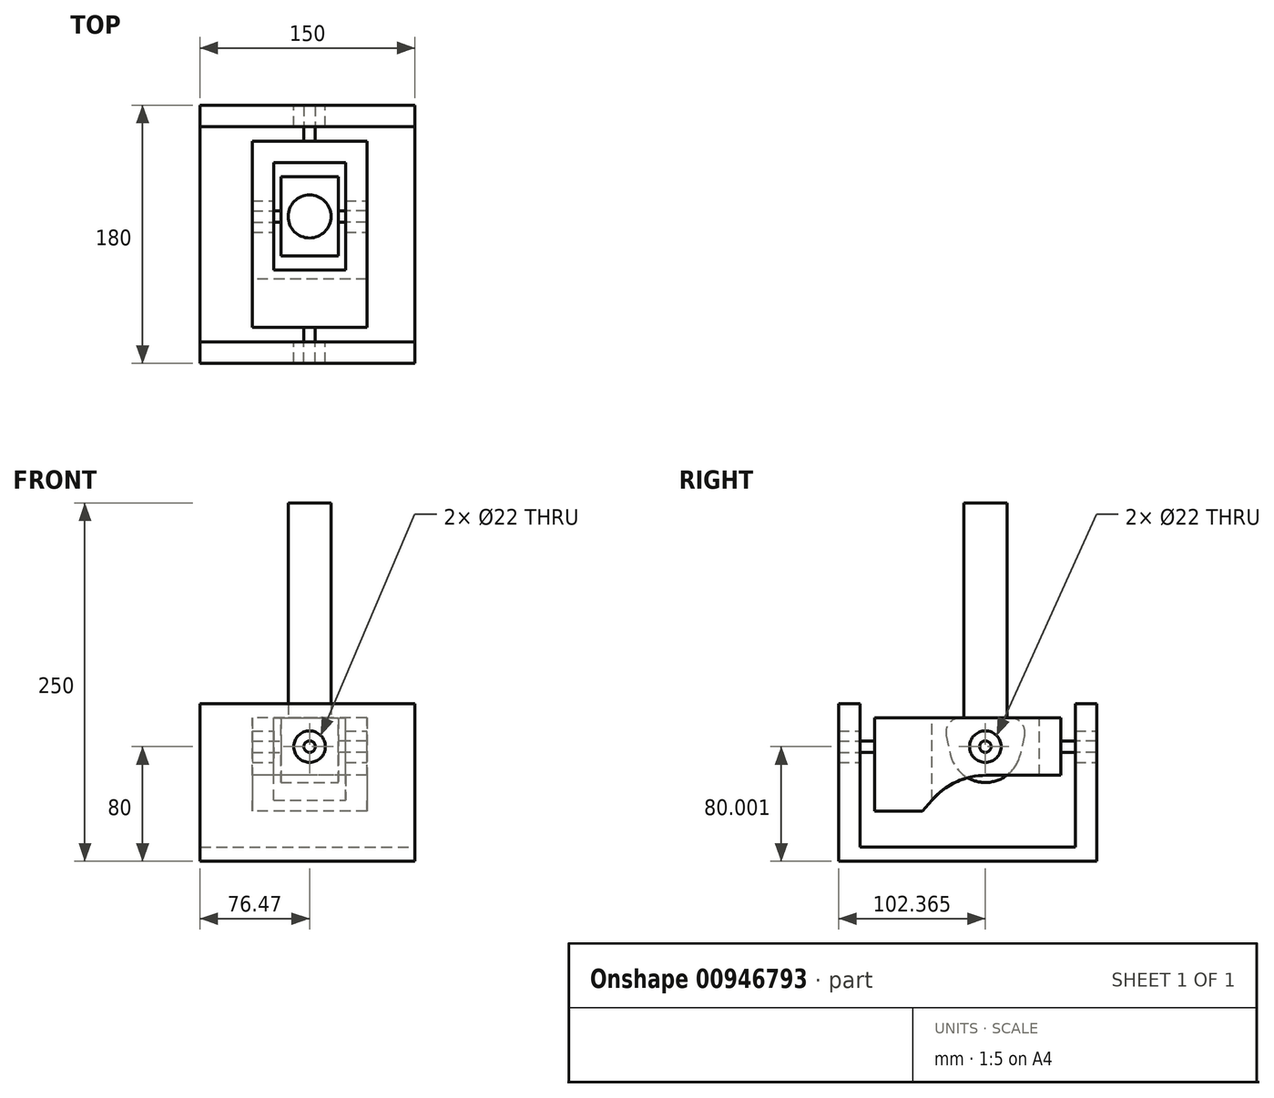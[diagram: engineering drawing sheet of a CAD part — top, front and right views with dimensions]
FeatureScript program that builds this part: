
annotation { "Feature Type Name" : "Feature", "Feature Type Description" : "" }
export const myFeature = defineFeature(function(context is Context, id is Id, definition is map)
    precondition{}
    {
        {
            var Q0;
            Q0=qCreatedBy(makeId("Top.planeOp"),FACE);
            var sketch = newSketch(context, id + "F0", { "sketchPlane" : qUnion([Q0])});
            skLineSegment(sketch, "E0", {"start": v(-76.47, 69.91) * mm, "end": v(-76.47, -110.09) * mm});
            skLineSegment(sketch, "E1", {"start": v(-76.47, -110.09) * mm, "end": v(73.53, -110.09) * mm});
            skLineSegment(sketch, "E2", {"start": v(73.53, -110.09) * mm, "end": v(73.53, 69.91) * mm});
            skLineSegment(sketch, "E3", {"start": v(73.53, 69.91) * mm, "end": v(-76.47, 69.91) * mm});
            skSolve(sketch);
        }
        {
            var Q0;
            Q0=makeQuery(id+"F0.imprint","IMPRINT",FACE,{"disambiguationData":[TD([[makeQuery(id+"F0.imprint","IMPRINT",EDGE,{"derivedFrom":sQuery(id+"F0.wireOp",EDGE,"E0")}),1.0]])]});
            extrude(context, id + "F1", {"entities" : qUnion([Q0]), "depth" : 10 * mm, "offsetDistance" : 25.4 * mm});
        }
        {
            var Q0;
            Q0=makeQuery(id+"F1.opExtrude","CAP_FACE",FACE,{"disambiguationData":[OSD([sQuery(id+"F0.wireOp",EDGE,"E0"),sQuery(id+"F0.wireOp",EDGE,"E1"),sQuery(id+"F0.wireOp",EDGE,"E2"),sQuery(id+"F0.wireOp",EDGE,"E3")])],"isStart":false});
            var sketch = newSketch(context, id + "F2", { "sketchPlane" : qUnion([Q0])});
            skLineSegment(sketch, "E4", {"start": v(73.53, 54.91) * mm, "end": v(-76.47, 54.91) * mm});
            skLineSegment(sketch, "E5", {"start": v(-76.47, -95.09) * mm, "end": v(73.53, -95.09) * mm});
            skSolve(sketch);
        }
        {
            var Q0;
            {var subQ0=sQuery(id+"F2.wireOp",EDGE,"E4");Q0=makeQuery(id+"F2.imprint","IMPRINT",FACE,{"disambiguationData":[TD([[makeQuery(id+"F2.imprint","IMPRINT",EDGE,{"derivedFrom":subQ0}),-1.0]])]});}
            var Q1;
            {var subQ0=sQuery(id+"F2.wireOp",EDGE,"E5");Q1=makeQuery(id+"F2.imprint","IMPRINT",FACE,{"disambiguationData":[TD([[makeQuery(id+"F2.imprint","IMPRINT",EDGE,{"derivedFrom":subQ0}),-1.0]])]});}
            extrude(context, id + "F3", {"entities" : qUnion([Q0, Q1]), "operationType" : NewBodyOperationType.ADD, "depth" : 100 * mm, "offsetDistance" : 25.4 * mm});
        }
        {
            var Q0;
            {var subQ0=sQuery(id+"F0.wireOp",EDGE,"E3");Q0=makeQuery(id+"F3.boolean.opBoolean","MERGE",FACE,{"derivedFrom":[makeQuery(id+"F1.opExtrude","SWEPT_FACE",FACE,{"disambiguationData":[OSD([subQ0])]}),makeQuery(id+"F3.opExtrude","SWEPT_FACE",FACE,{"disambiguationData":[OSD([subQ0])]})]});}
            var sketch = newSketch(context, id + "F4", { "sketchPlane" : qUnion([Q0])});
            skCircle(sketch, "E6", {"center": v(0, 80) * mm, "radius": 11 * mm});
            skSolve(sketch);
        }
        {
            var Q0;
            Q0=sQuery(id+"F4.wireOp",VERTEX,"E6.center");
            var Q1;
            Q1=makeQuery(id+"F1.opExtrude","SWEPT_BODY",BODY,{"disambiguationData":[OSD([sQuery(id+"F0.wireOp",EDGE,"E0"),sQuery(id+"F0.wireOp",EDGE,"E1"),sQuery(id+"F0.wireOp",EDGE,"E2"),sQuery(id+"F0.wireOp",EDGE,"E3")])]});
            hole(context, id + "F5", {"style" : HoleStyle.SIMPLE, "endStyle" : HoleEndStyle.THROUGH, "holeDiameter" : 22 * mm, "majorDiameter" : 6.35 * mm, "isTappedThrough" : true, "tappedDepth" : 12.7 * mm, "tapClearance" : 3, "locations" : qUnion([Q0]), "scope" : qUnion([Q1])});
        }
        {
            var Q0;
            Q0=qCreatedBy(makeId("Right.planeOp"),FACE);
            var sketch = newSketch(context, id + "F6", { "sketchPlane" : qUnion([Q0])});
            skLineSegment(sketch, "E7", {"start": v(-85.09, 100) * mm, "end": v(-85.09, 35) * mm});
            skLineSegment(sketch, "E8", {"start": v(-85.09, 35) * mm, "end": v(44.91, 35) * mm});
            skLineSegment(sketch, "E9", {"start": v(44.91, 35) * mm, "end": v(44.91, 100) * mm});
            skLineSegment(sketch, "E10", {"start": v(44.91, 100) * mm, "end": v(-85.09, 100) * mm});
            skLineSegment(sketch, "E11", {"start": v(-51.54, 35) * mm, "end": v(-45.05, 42.56) * mm});
            skLineSegment(sketch, "E12", {"start": v(-7.1, 60) * mm, "end": v(44.91, 60) * mm});
            skPoint(sketch, "E12.endSnap0", {"position": v(44.91, 67.5) * mm});
            skPoint(sketch, "E13.visualSharp", {"position": v(-30.09, 60) * mm});
            skArc(sketch, "E13.filletArc", {"start": v(-7.1, 60) * mm, "mid": v(-27.99, 55.43) * mm, "end": v(-45.05, 42.56) * mm});
            skSolve(sketch);
        }
        {
            var Q0;
            {var subQ4=sQuery(id+"F6.wireOp",EDGE,"E7");Q0=makeQuery(id+"F6.imprint","IMPRINT",FACE,{"disambiguationData":[TD([[makeQuery(id+"F6.imprint","IMPRINT",EDGE,{"derivedFrom":subQ4}),1.0]])]});}
            extrude(context, id + "F7", {"entities" : qUnion([Q0]), "depth" : 40 * mm, "offsetDistance" : 25.4 * mm});
        }
        {
            var Q0;
            Q0=makeQuery(id+"F7.opExtrude","SWEPT_BODY",BODY,{"disambiguationData":[OSD([sQuery(id+"F6.wireOp",EDGE,"E7"),sQuery(id+"F6.wireOp",EDGE,"E8"),sQuery(id+"F6.wireOp",EDGE,"E9"),sQuery(id+"F6.wireOp",EDGE,"E10"),sQuery(id+"F6.wireOp",EDGE,"E11"),sQuery(id+"F6.wireOp",EDGE,"E12"),sQuery(id+"F6.wireOp",EDGE,"E13.filletArc")])]});
            var Q1;
            Q1=qCreatedBy(makeId("Right.planeOp"),FACE);
            mirror(context, id + "F8", {"operationType" : NewBodyOperationType.ADD, "entities" : qUnion([Q0]), "mirrorPlane" : qUnion([Q1])});
        }
        {
            var Q0;
            {var subQ0=makeQuery(id+"F7.opExtrude","SWEPT_FACE",FACE,{"disambiguationData":[OSD([sQuery(id+"F6.wireOp",EDGE,"E7")])]});Q0=makeQuery(id+"F8.boolean.opBoolean","MERGE",FACE,{"derivedFrom":[subQ0,makeQuery(id+"F8.opPattern","COPY",FACE,{"derivedFrom":subQ0,"instanceName":"1"})]});}
            var sketch = newSketch(context, id + "F9", { "sketchPlane" : qUnion([Q0])});
            skCircle(sketch, "E14", {"center": v(0, 80.04) * mm, "radius": 4 * mm});
            skSolve(sketch);
        }
        {
            var Q0;
            Q0=makeQuery(id+"F9.imprint","IMPRINT",FACE,{"disambiguationData":[TD([[makeQuery(id+"F9.imprint","IMPRINT",EDGE,{"derivedFrom":sQuery(id+"F9.wireOp",EDGE,"E14")}),1.0]])]});
            extrude(context, id + "F10", {"entities" : qUnion([Q0]), "operationType" : NewBodyOperationType.ADD, "depth" : 25 * mm, "offsetDistance" : 25.4 * mm});
        }
        {
            var Q0;
            {var subQ0=makeQuery(id+"F7.opExtrude","SWEPT_FACE",FACE,{"disambiguationData":[OSD([sQuery(id+"F6.wireOp",EDGE,"E9")])]});Q0=makeQuery(id+"F8.boolean.opBoolean","MERGE",FACE,{"derivedFrom":[subQ0,makeQuery(id+"F8.opPattern","COPY",FACE,{"derivedFrom":subQ0,"instanceName":"1"})]});}
            var sketch = newSketch(context, id + "F11", { "sketchPlane" : qUnion([Q0])});
            skCircle(sketch, "E15", {"center": v(0, 80) * mm, "radius": 4 * mm});
            skPoint(sketch, "E15.centerSnap0", {"position": v(-40, 80) * mm});
            skSolve(sketch);
        }
        {
            var Q0;
            Q0=makeQuery(id+"F11.imprint","IMPRINT",FACE,{"disambiguationData":[TD([[makeQuery(id+"F11.imprint","IMPRINT",EDGE,{"derivedFrom":sQuery(id+"F11.wireOp",EDGE,"E15")}),1.0]])]});
            extrude(context, id + "F12", {"entities" : qUnion([Q0]), "operationType" : NewBodyOperationType.ADD, "depth" : 25 * mm, "offsetDistance" : 25.4 * mm});
        }
        {
            var Q0;
            {var subQ0=makeQuery(id+"F7.opExtrude","SWEPT_FACE",FACE,{"disambiguationData":[OSD([sQuery(id+"F6.wireOp",EDGE,"E10")])]});Q0=makeQuery(id+"F8.boolean.opBoolean","MERGE",FACE,{"derivedFrom":[subQ0,makeQuery(id+"F8.opPattern","COPY",FACE,{"derivedFrom":subQ0,"instanceName":"1"})]});}
            var sketch = newSketch(context, id + "F13", { "sketchPlane" : qUnion([Q0])});
            skLineSegment(sketch, "E16", {"start": v(-25, -45.09) * mm, "end": v(25, -45.09) * mm});
            skLineSegment(sketch, "E17", {"start": v(25, -45.09) * mm, "end": v(25, 29.91) * mm});
            skLineSegment(sketch, "E18", {"start": v(25, 29.91) * mm, "end": v(-25, 29.91) * mm});
            skLineSegment(sketch, "E19", {"start": v(-25, 29.91) * mm, "end": v(-25, -45.09) * mm});
            skSolve(sketch);
        }
        {
            var Q0;
            Q0=makeQuery(id+"F13.imprint","IMPRINT",FACE,{"disambiguationData":[TD([[makeQuery(id+"F13.imprint","IMPRINT",EDGE,{"derivedFrom":sQuery(id+"F13.wireOp",EDGE,"E16")}),1.0]])]});
            extrude(context, id + "F14", {"entities" : qUnion([Q0]), "operationType" : NewBodyOperationType.REMOVE, "oppositeDirection" : true, "depth" : 65.28 * mm, "offsetDistance" : 25.4 * mm});
        }
        {
            var Q0;
            {var subQ0=makeQuery(id+"F7.opExtrude","SWEPT_FACE",FACE,{"disambiguationData":[OSD([sQuery(id+"F6.wireOp",EDGE,"E10")])]});Q0=makeQuery(id+"F8.boolean.opBoolean","MERGE",FACE,{"derivedFrom":[subQ0,makeQuery(id+"F8.opPattern","COPY",FACE,{"derivedFrom":subQ0,"instanceName":"1"})]});}
            var sketch = newSketch(context, id + "F15", { "sketchPlane" : qUnion([Q0])});
            skLineSegment(sketch, "E20", {"start": v(25, -7.59) * mm, "end": v(40, -7.59) * mm});
            skSolve(sketch);
        }
        {
            var Q0;
            Q0=makeQuery(id+"F7.opExtrude","CAP_FACE",FACE,{"disambiguationData":[OSD([sQuery(id+"F6.wireOp",EDGE,"E7"),sQuery(id+"F6.wireOp",EDGE,"E8"),sQuery(id+"F6.wireOp",EDGE,"E9"),sQuery(id+"F6.wireOp",EDGE,"E10"),sQuery(id+"F6.wireOp",EDGE,"E11"),sQuery(id+"F6.wireOp",EDGE,"E12"),sQuery(id+"F6.wireOp",EDGE,"E13.filletArc")])],"isStart":false});
            var sketch = newSketch(context, id + "F16", { "sketchPlane" : qUnion([Q0])});
            skCircle(sketch, "E21", {"center": v(-7.72, 80) * mm, "radius": 11 * mm});
            skSolve(sketch);
        }
        {
            var Q0;
            Q0=makeQuery(id+"F16.imprint","IMPRINT",FACE,{"disambiguationData":[TD([[makeQuery(id+"F16.imprint","IMPRINT",EDGE,{"derivedFrom":sQuery(id+"F16.wireOp",EDGE,"E21")}),1.0]])]});
            extrude(context, id + "F17", {"entities" : qUnion([Q0]), "operationType" : NewBodyOperationType.REMOVE, "oppositeDirection" : true, "depth" : 87.12 * mm, "offsetDistance" : 25.4 * mm});
        }
        {
            var Q0;
            Q0=makeQuery(id+"F7.opExtrude","CAP_FACE",FACE,{"disambiguationData":[OSD([sQuery(id+"F6.wireOp",EDGE,"E7"),sQuery(id+"F6.wireOp",EDGE,"E8"),sQuery(id+"F6.wireOp",EDGE,"E9"),sQuery(id+"F6.wireOp",EDGE,"E10"),sQuery(id+"F6.wireOp",EDGE,"E11"),sQuery(id+"F6.wireOp",EDGE,"E12"),sQuery(id+"F6.wireOp",EDGE,"E13.filletArc")])],"isStart":false});
            var sketch = newSketch(context, id + "F18", { "sketchPlane" : qUnion([Q0])});
            skCircle(sketch, "E22", {"center": v(-7.72, 80) * mm, "radius": 4 * mm});
            skSolve(sketch);
        }
        {
            var Q0;
            {var subQ1=sQuery(id+"F6.wireOp",EDGE,"E10");var subQ6=makeQuery(id+"F7.opExtrude","CAP_EDGE",EDGE,{"disambiguationData":[OSD([subQ1])],"isStart":false});Q0=makeQuery(id+"F15.imprint","IMPRINT",FACE,{"disambiguationData":[TD([[makeQuery(id+"F15.imprint","IMPRINT",EDGE,{"derivedFrom":makeQuery(id+"F8.opPattern","COPY",EDGE,{"derivedFrom":subQ6,"instanceName":"1"})}),1.0]])]});}
            var sketch = newSketch(context, id + "F19", { "sketchPlane" : qUnion([Q0])});
            skLineSegment(sketch, "E23", {"start": v(-20, 22.41) * mm, "end": v(20, 22.41) * mm});
            skLineSegment(sketch, "E24", {"start": v(20, 22.41) * mm, "end": v(20, -37.59) * mm});
            skLineSegment(sketch, "E25", {"start": v(20, -37.59) * mm, "end": v(-20, -37.59) * mm});
            skLineSegment(sketch, "E26", {"start": v(-20, -37.59) * mm, "end": v(-20, 22.41) * mm});
            skSolve(sketch);
        }
        {
            var Q0;
            Q0=makeQuery(id+"F19.imprint","IMPRINT",FACE,{"disambiguationData":[TD([[makeQuery(id+"F19.imprint","IMPRINT",EDGE,{"derivedFrom":sQuery(id+"F19.wireOp",EDGE,"E23")}),-1.0]])]});
            extrude(context, id + "F20", {"entities" : qUnion([Q0]), "oppositeDirection" : true, "depth" : 45 * mm, "offsetDistance" : 25.4 * mm});
        }
        {
            var Q0;
            Q0=makeQuery(id+"F20.opExtrude","SWEPT_FACE",FACE,{"disambiguationData":[OSD([sQuery(id+"F19.wireOp",EDGE,"E24")])]});
            var sketch = newSketch(context, id + "F21", { "sketchPlane" : qUnion([Q0])});
            skPoint(sketch, "E27.endSnap0", {"position": v(-7.59, 55) * mm});
            skPoint(sketch, "E28", {"position": v(-7.72, 80) * mm});
            skCircle(sketch, "E29", {"center": v(-7.72, 80) * mm, "radius": 25 * mm});
            skLineSegment(sketch, "E30", {"start": v(19.66, 87.8) * mm, "end": v(16.66, 74.5) * mm});
            skLineSegment(sketch, "E31", {"start": v(-34.99, 87.9) * mm, "end": v(-32.17, 74.76) * mm});
            skLineSegment(sketch, "E32", {"start": v(-25.21, 100) * mm, "end": v(9.9, 100) * mm});
            skPoint(sketch, "E33.visualSharp", {"position": v(-37.59, 100) * mm});
            skArc(sketch, "E33.filletArc", {"start": v(-25.21, 100) * mm, "mid": v(-32.99, 96.29) * mm, "end": v(-34.99, 87.9) * mm});
            skPoint(sketch, "E34.visualSharp", {"position": v(22.41, 100) * mm});
            skArc(sketch, "E34.filletArc", {"start": v(19.66, 87.8) * mm, "mid": v(17.72, 96.24) * mm, "end": v(9.9, 100) * mm});
            skLineSegment(sketch, "E35", {"start": v(-32.17, 74.76) * mm, "end": v(16.66, 74.5) * mm});
            skSolve(sketch);
        }
        {
            var Q0;
            {var subQ1=sQuery(id+"F21.wireOp",EDGE,"E30");Q0=makeQuery(id+"F21.imprint","IMPRINT",FACE,{"disambiguationData":[TD([[makeQuery(id+"F21.imprint","IMPRINT",EDGE,{"derivedFrom":subQ1}),1.0]])]});}
            var Q1;
            {var subQ3=sQuery(id+"F21.wireOp",EDGE,"E31");Q1=makeQuery(id+"F21.imprint","IMPRINT",FACE,{"disambiguationData":[TD([[makeQuery(id+"F21.imprint","IMPRINT",EDGE,{"derivedFrom":subQ3}),-1.0]])]});}
            extrude(context, id + "F22", {"entities" : qUnion([Q0, Q1]), "operationType" : NewBodyOperationType.REMOVE, "oppositeDirection" : true, "depth" : 42.67 * mm, "offsetDistance" : 25.4 * mm});
        }
        {
            var Q0;
            Q0=makeQuery(id+"F20.opExtrude","SWEPT_FACE",FACE,{"disambiguationData":[OSD([sQuery(id+"F19.wireOp",EDGE,"E24")])]});
            var sketch = newSketch(context, id + "F23", { "sketchPlane" : qUnion([Q0])});
            skPoint(sketch, "E36", {"position": v(-7.72, 80) * mm});
            skCircle(sketch, "E37", {"center": v(-7.72, 80) * mm, "radius": 4 * mm});
            skSolve(sketch);
        }
        {
            var Q0;
            Q0=makeQuery(id+"F23.imprint","IMPRINT",FACE,{"disambiguationData":[TD([[makeQuery(id+"F23.imprint","IMPRINT",EDGE,{"derivedFrom":sQuery(id+"F23.wireOp",EDGE,"E37")}),1.0]])]});
            extrude(context, id + "F24", {"entities" : qUnion([Q0]), "operationType" : NewBodyOperationType.ADD, "depth" : 20 * mm, "offsetDistance" : 25.4 * mm});
        }
        {
            var Q0;
            Q0=makeQuery(id+"F20.opExtrude","SWEPT_FACE",FACE,{"disambiguationData":[OSD([sQuery(id+"F19.wireOp",EDGE,"E26")])]});
            var sketch = newSketch(context, id + "F25", { "sketchPlane" : qUnion([Q0])});
            skPoint(sketch, "E38", {"position": v(7.72, 80) * mm});
            skCircle(sketch, "E39", {"center": v(7.72, 80) * mm, "radius": 4 * mm});
            skSolve(sketch);
        }
        {
            var Q0;
            Q0=makeQuery(id+"F25.imprint","IMPRINT",FACE,{"disambiguationData":[TD([[makeQuery(id+"F25.imprint","IMPRINT",EDGE,{"derivedFrom":sQuery(id+"F25.wireOp",EDGE,"E39")}),1.0]])]});
            extrude(context, id + "F26", {"entities" : qUnion([Q0]), "operationType" : NewBodyOperationType.ADD, "depth" : 20 * mm, "offsetDistance" : 25.4 * mm});
        }
        {
            var Q0;
            Q0=makeQuery(id+"F20.opExtrude","CAP_FACE",FACE,{"disambiguationData":[OSD([sQuery(id+"F19.wireOp",EDGE,"E23"),sQuery(id+"F19.wireOp",EDGE,"E24"),sQuery(id+"F19.wireOp",EDGE,"E25"),sQuery(id+"F19.wireOp",EDGE,"E26")])],"isStart":true});
            var sketch = newSketch(context, id + "F27", { "sketchPlane" : qUnion([Q0])});
            skCircle(sketch, "E40", {"center": v(0, -7.65) * mm, "radius": 15 * mm});
            skPoint(sketch, "E40.centerSnap0", {"position": v(-20, -7.65) * mm});
            skSolve(sketch);
        }
        {
            var Q0;
            Q0=makeQuery(id+"F27.imprint","IMPRINT",FACE,{"disambiguationData":[TD([[makeQuery(id+"F27.imprint","IMPRINT",EDGE,{"derivedFrom":sQuery(id+"F27.wireOp",EDGE,"E40")}),1.0]])]});
            extrude(context, id + "F28", {"entities" : qUnion([Q0]), "operationType" : NewBodyOperationType.ADD, "depth" : 150 * mm, "offsetDistance" : 25.4 * mm});
        }
    });
